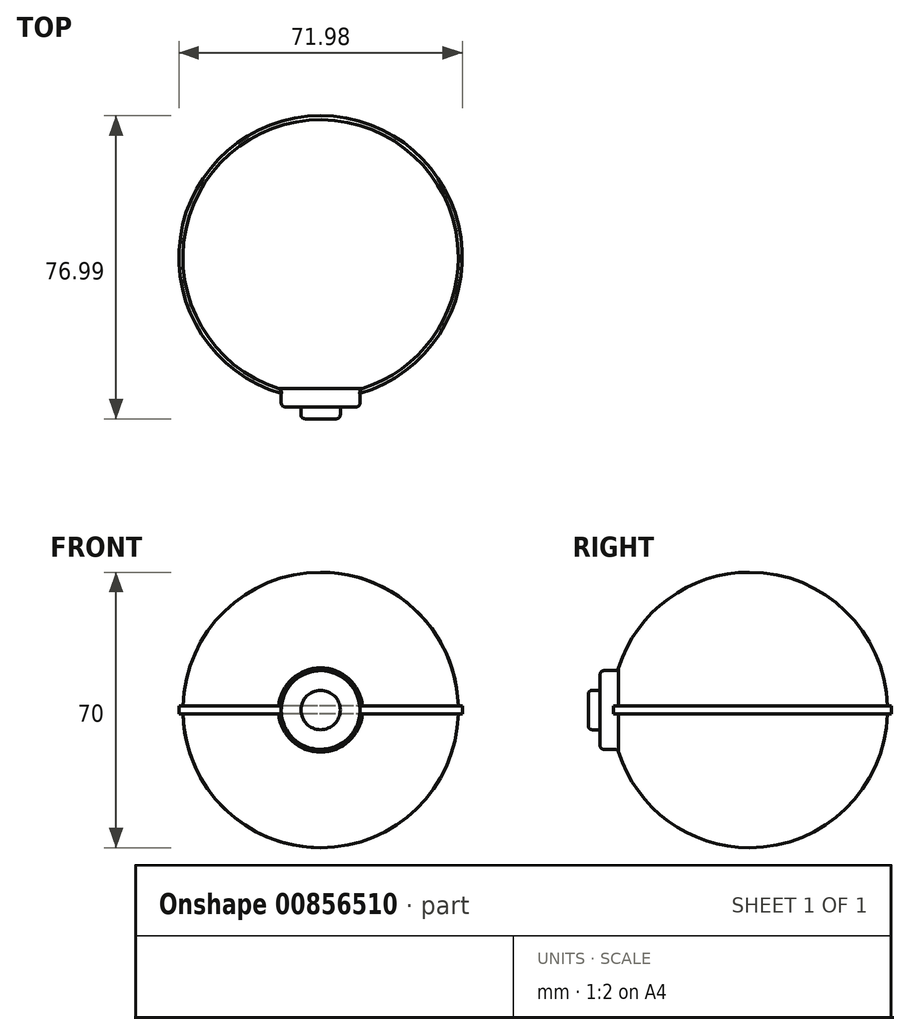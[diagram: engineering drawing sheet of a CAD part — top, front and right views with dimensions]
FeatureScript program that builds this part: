
annotation { "Feature Type Name" : "Feature", "Feature Type Description" : "" }
export const myFeature = defineFeature(function(context is Context, id is Id, definition is map)
    precondition{}
    {
        {
            var Q0;
            Q0=qCreatedBy(makeId("Front.planeOp"),FACE);
            var sketch = newSketch(context, id + "F0", { "sketchPlane" : qUnion([Q0])});
            skLineSegment(sketch, "E0", {"start": v(0, 35) * mm, "end": v(0, 0) * mm});
            skArc(sketch, "E1", {"start": v(0, 35) * mm, "mid": v(-24.4, 25.1) * mm, "end": v(-34.99, 1) * mm});
            skLineSegment(sketch, "E2", {"start": v(0, -35) * mm, "end": v(0, 0) * mm});
            skLineSegment(sketch, "E3.bottom", {"start": v(-34.99, 1) * mm, "end": v(-35.99, 1) * mm});
            skLineSegment(sketch, "E3.top", {"start": v(-34.99, -1) * mm, "end": v(-35.99, -1) * mm});
            skLineSegment(sketch, "E3.left", {"start": v(0, 1) * mm, "end": v(0, -1) * mm});
            skLineSegment(sketch, "E3.right", {"start": v(-35.99, 1) * mm, "end": v(-35.99, -1) * mm});
            skArc(sketch, "E4.trimOffspring", {"start": v(-34.99, -1) * mm, "mid": v(-24.4, -25.1) * mm, "end": v(0, -35) * mm});
            skSolve(sketch);
        }
        {
            var Q0;
            Q0=makeQuery(id+"F0.imprint","IMPRINT",FACE,{"disambiguationData":[TD([[makeQuery(id+"F0.imprint","IMPRINT",EDGE,{"derivedFrom":sQuery(id+"F0.wireOp",EDGE,"E0")}),-1.0]])]});
            var Q1;
            Q1=sQuery(id+"F0.wireOp",EDGE,"E1");
            var Q2;
            Q2=sQuery(id+"F0.wireOp",EDGE,"E0");
            revolve(context, id + "F1", {"surfaceOperationType" : NewSurfaceOperationType.NEW, "entities" : qUnion([Q0]), "surfaceEntities" : qUnion([Q1]), "axis" : qUnion([Q2]), "revolveType" : RevolveType.FULL});
        }
        {
            var Q0;
            Q0=qCreatedBy(makeId("Front.planeOp"),FACE);
            var sketch = newSketch(context, id + "F2", { "sketchPlane" : qUnion([Q0])});
            skCircle(sketch, "E5", {"center": v(0, 0) * mm, "radius": 10 * mm});
            skSolve(sketch);
        }
        {
            var Q0;
            Q0 = qSketchRegion(id + "F2", true);
            var Q1;
            Q1=sQuery(id+"F2.wireOp",EDGE,"E5");
            extrude(context, id + "F3", {"entities" : qUnion([Q0]), "operationType" : NewBodyOperationType.ADD, "surfaceEntities" : qUnion([Q1]), "depth" : 38 * mm, "offsetDistance" : 25 * mm});
        }
        {
            var Q0;
            Q0=makeQuery(id+"F3.opExtrude","CAP_FACE",FACE,{"disambiguationData":[OSD([sQuery(id+"F2.wireOp",EDGE,"E5")])],"isStart":false});
            var sketch = newSketch(context, id + "F4", { "sketchPlane" : qUnion([Q0])});
            skCircle(sketch, "E6", {"center": v(0, 0) * mm, "radius": 5 * mm});
            skSolve(sketch);
        }
        {
            var Q0;
            Q0 = qSketchRegion(id + "F4", true);
            var sketch = newSketch(context, id + "F5", { "sketchPlane" : qUnion([Q0])});
            skSolve(sketch);
        }
        {
            var Q0;
            Q0=makeQuery(id+"F5.imprint","IMPRINT",FACE,{"disambiguationData":[TD([[makeQuery(id+"F5.imprint","IMPRINT",EDGE,{"derivedFrom":makeQuery(id+"F4.imprint","IMPRINT",EDGE,{"derivedFrom":sQuery(id+"F4.wireOp",EDGE,"E6")})}),1.0]])]});
            extrude(context, id + "F6", {"entities" : qUnion([Q0]), "operationType" : NewBodyOperationType.ADD, "depth" : 3 * mm, "offsetDistance" : 25 * mm});
        }
        {
            var Q0;
            Q0=makeQuery(id+"F6.opExtrude","CAP_EDGE",EDGE,{"disambiguationData":[OSD([sQuery(id+"F4.wireOp",EDGE,"E6")])],"isStart":false});
            var Q1;
            Q1=makeQuery(id+"F6.opExtrude","CAP_EDGE",EDGE,{"disambiguationData":[OSD([sQuery(id+"F4.wireOp",EDGE,"E6")])],"isStart":true});
            var Q2;
            Q2=makeQuery(id+"F3.opExtrude","CAP_EDGE",EDGE,{"disambiguationData":[OSD([sQuery(id+"F2.wireOp",EDGE,"E5")])],"isStart":false});
            var Q3;
            Q3=makeQuery(id+"F3.boolean.opBoolean","INTERSECT",EDGE,{"derivedFrom":[makeQuery(id+"F1.opRevolve","SWEPT_FACE",FACE,{"disambiguationData":[OSD([sQuery(id+"F0.wireOp",EDGE,"E1")])]}),makeQuery(id+"F3.opExtrude","SWEPT_FACE",FACE,{"disambiguationData":[OSD([sQuery(id+"F2.wireOp",EDGE,"E5")])]})]});
            var Q4;
            Q4=makeQuery(id+"F3.boolean.opBoolean","INTERSECT",EDGE,{"derivedFrom":[makeQuery(id+"F1.opRevolve","SWEPT_FACE",FACE,{"disambiguationData":[OSD([sQuery(id+"F0.wireOp",EDGE,"E4.trimOffspring")])]}),makeQuery(id+"F3.opExtrude","SWEPT_FACE",FACE,{"disambiguationData":[OSD([sQuery(id+"F2.wireOp",EDGE,"E5")])]})]});
            fillet(context, id + "F7", {"entities" : qUnion([Q0, Q1, Q2, Q3, Q4]), "radius" : 1 * mm, "tangentPropagation" : true, "allowEdgeOverflow" : false});
        }
    });
